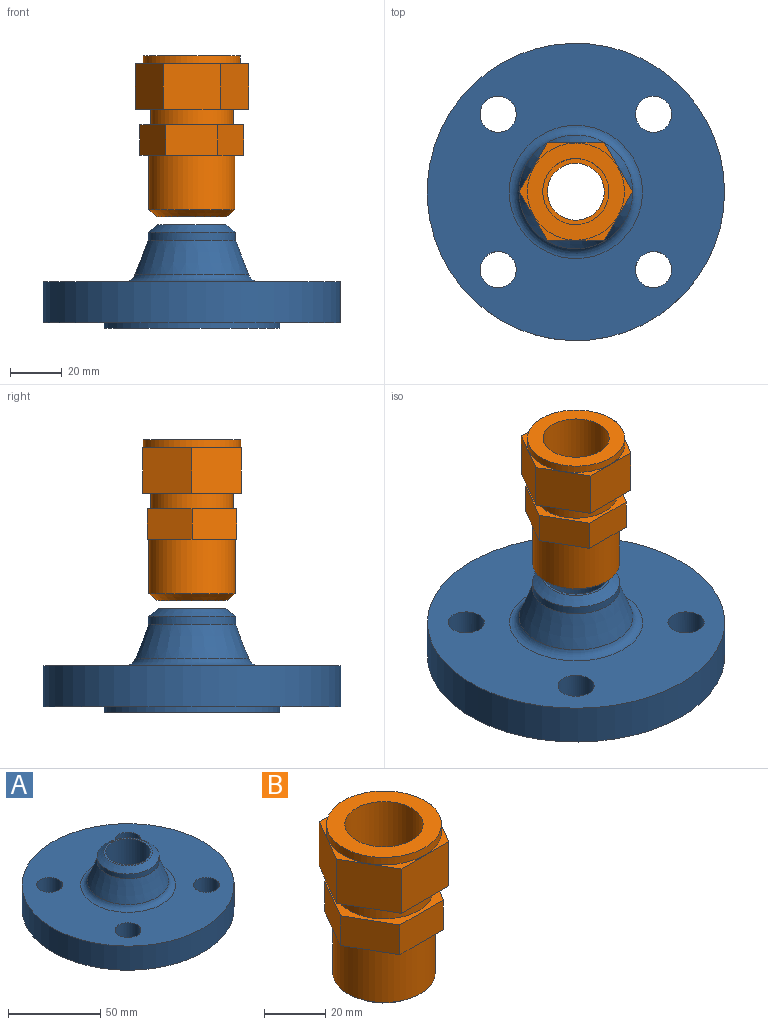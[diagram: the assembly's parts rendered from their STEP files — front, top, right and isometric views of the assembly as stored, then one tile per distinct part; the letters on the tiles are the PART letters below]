
ASSEMBLY  parts=2 mates=1
PART A: 16 faces, bbox 115x115x40 mm
  f0: plane 26.25x26.25mm, normal (0,0,1), area 79.3mm2, adj f1,f13
  f1: cylinder r=12.12mm len=40mm, axis (0,0,1), area 3047.3mm2, adj f0,f2
  f2: plane 68x68mm, normal (0,0,-1), area 3169.8mm2, adj f1,f3
  f3: cylinder r=34mm len=68mm, axis (0,0,1), area 427.3mm2, adj f2,f4
  f4: plane 115x115mm, normal (0,0,-1), area 6139.5mm2, adj f3,f5,f9,f10,f11,f12
  f5: cylinder r=57.5mm len=115mm, axis (0,0,1), area 5780.5mm2, adj f4,f6
  f6: plane 115x115mm, normal (0,0,1), area 7688.4mm2, adj f5,f9,f10,f11,f12,f15
  f7: cone r=23mm half-angle=21deg, axis (0,0,-1), area 1757.4mm2, adj f8,f15
  f8: cylinder r=16.85mm len=33.7mm, axis (0,0,1), area 332.5mm2, adj f7,f14
  f9: cylinder r=7mm len=16mm, axis (0,0,1), area 703.7mm2, adj f4,f6
  f10: cylinder r=7mm len=16mm, axis (0,0,1), area 703.7mm2, adj f4,f6
  f11: cylinder r=7mm len=16mm, axis (0,0,1), area 703.7mm2, adj f4,f6
  f12: cylinder r=7mm len=16mm, axis (0,0,1), area 703.7mm2, adj f4,f6
  f13: cylinder r=13.12mm len=26.25mm, axis (0,0,-1), area 0.1mm2, adj f0,f14
  f14: cone r=13.12mm half-angle=52.5deg, axis (0,0,-1), area 442.1mm2, adj f8,f13
  f15: torus R=25.75mm, axis (0,0,-1), area 714.6mm2, adj f6,f7
PART B: 27 faces, bbox 43.9x38x62.3 mm
  f0: cylinder r=12.8mm len=31.4mm, axis (0,0,-1), area 2525.3mm2, adj f1,f14
  f1: plane 25.6x25.6mm, normal (0,0,1), area 134.6mm2, adj f0,f2
  f2: cylinder r=11mm len=22mm, axis (0,0,-1), area 124.4mm2, adj f1,f3
  f3: plane 24.25x24.25mm, normal (0,0,-1), area 81.7mm2, adj f2,f4
  f4: cylinder r=12.12mm len=29.1mm, axis (0,0,-1), area 2216.9mm2, adj f3,f5
  f5: plane 26.25x26.25mm, normal (0,0,-1), area 79.3mm2, adj f4,f6
  f6: cone r=13.12mm half-angle=52.5deg, axis (0,0,1), area 422.2mm2, adj f5,f7
  f7: cylinder r=16.7mm len=33.4mm, axis (0,0,-1), area 2209.5mm2, adj f6,f8
  f8: plane 40.18x34.8mm, normal (0,0,-1), area 172.6mm2, adj f7,f21,f22,f23,f24,f25,f26
  f9: plane 40.18x34.8mm, normal (0,0,1), area 244.5mm2, adj f10,f21,f22,f23,f24,f25,f26
  f10: cylinder r=16mm len=32mm, axis (0,0,-1), area 593.1mm2, adj f9,f11
  f11: plane 43.88x38mm, normal (0,0,-1), area 446.3mm2, adj f10,f15,f16,f17,f18,f19,f20
  f12: plane 43.88x38mm, normal (0,0,1), area 140.2mm2, adj f13,f15,f16,f17,f18,f19,f20
  f13: cylinder r=18.8mm len=37.6mm, axis (0,0,-1), area 354.4mm2, adj f12,f14
  f14: plane 37.6x37.6mm, normal (0,0,1), area 595.6mm2, adj f0,f13
  f15: plane 19x17.7mm, normal (-0.87,0.5,0), area 388.3mm2, adj f11,f12,f16,f20
  f16: plane 21.94x17.7mm, normal (0,1,0), area 388.3mm2, adj f11,f12,f15,f17
  f17: plane 19x17.7mm, normal (0.87,0.5,0), area 388.3mm2, adj f11,f12,f16,f18
  f18: plane 19x17.7mm, normal (0.87,-0.5,0), area 388.3mm2, adj f11,f12,f17,f19
  f19: plane 21.94x17.7mm, normal (0,-1,0), area 388.3mm2, adj f11,f12,f18,f20
  f20: plane 19x17.7mm, normal (-0.87,-0.5,0), area 388.3mm2, adj f11,f12,f15,f19
  f21: plane 20.09x11.9mm, normal (0,1,0), area 239.1mm2, adj f8,f9,f22,f26
  f22: plane 17.4x11.9mm, normal (0.87,0.5,0), area 239.1mm2, adj f8,f9,f21,f23
  f23: plane 17.4x11.9mm, normal (0.87,-0.5,0), area 239.1mm2, adj f8,f9,f22,f24
  f24: plane 20.09x11.9mm, normal (0,-1,0), area 239.1mm2, adj f8,f9,f23,f25
  f25: plane 17.4x11.9mm, normal (-0.87,-0.5,0), area 239.1mm2, adj f8,f9,f24,f26
  f26: plane 17.4x11.9mm, normal (-0.87,0.5,0), area 239.1mm2, adj f8,f9,f21,f25
PLACE A t=(-0.56,-0.25,-19.88)mm fixed
PLACE B t=(-0.56,-0.25,23.12)mm
MATE fastened B.f0 <-> A.f1  axis (0,0,1) through (-0.56,-0.25,23.12)mm
